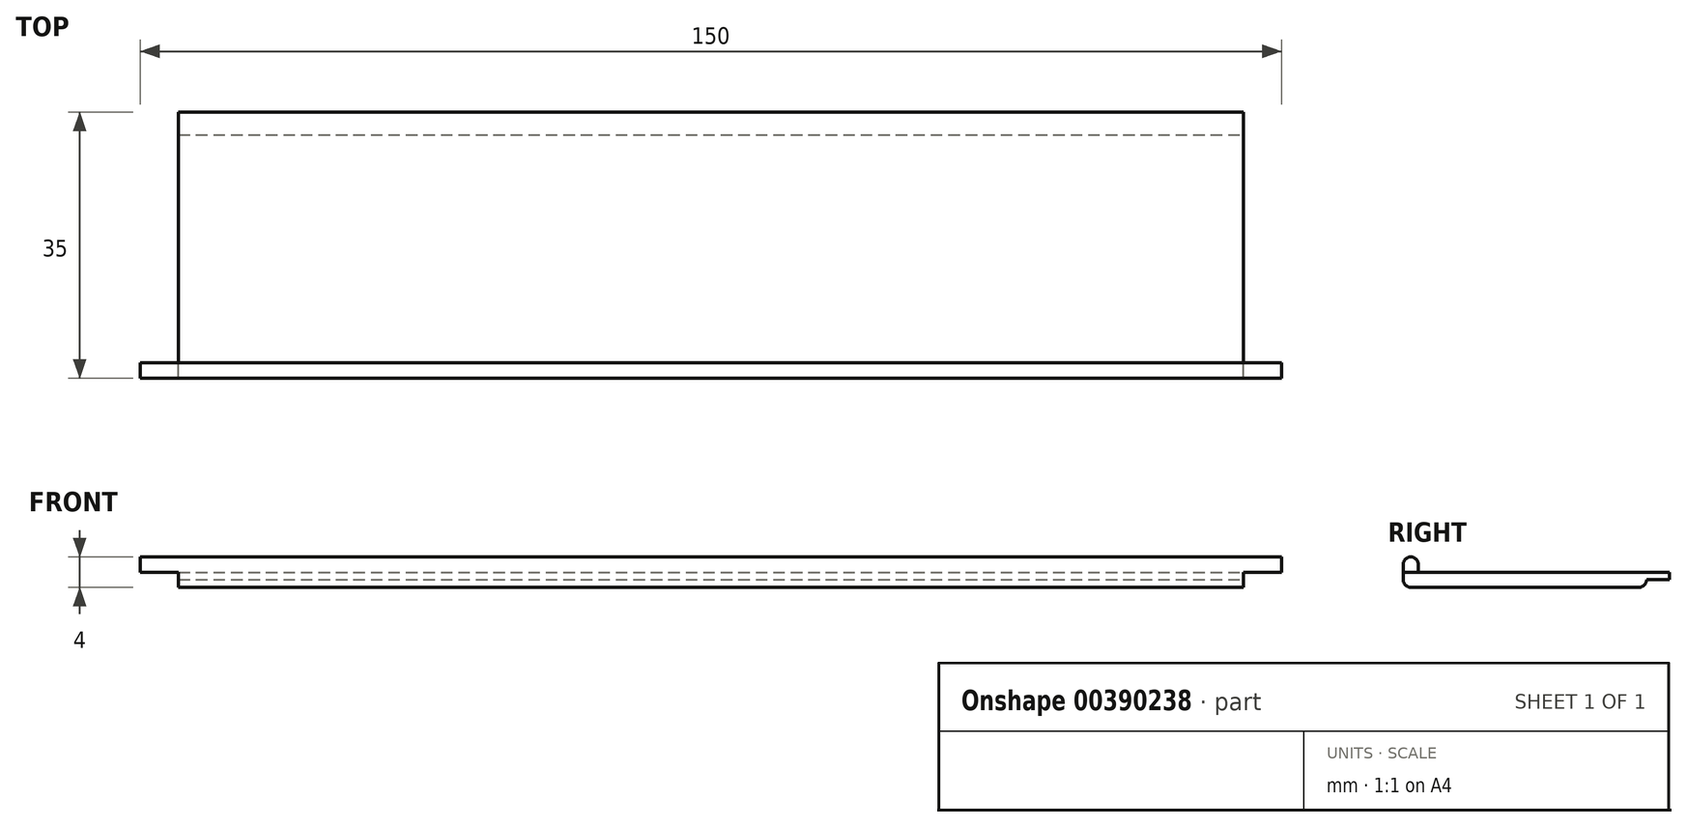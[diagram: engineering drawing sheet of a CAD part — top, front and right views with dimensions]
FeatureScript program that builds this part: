
annotation { "Feature Type Name" : "Feature", "Feature Type Description" : "" }
export const myFeature = defineFeature(function(context is Context, id is Id, definition is map)
    precondition{}
    {
        {
            var Q0;
            Q0=qCreatedBy(makeId("Right.planeOp"),FACE);
            var sketch = newSketch(context, id + "F0", { "sketchPlane" : qUnion([Q0])});
            skLineSegment(sketch, "E0.bottom", {"start": v(1, 0) * mm, "end": v(31, 0) * mm});
            skLineSegment(sketch, "E0.left", {"start": v(0, 1) * mm, "end": v(0, 1) * mm});
            skLineSegment(sketch, "E0.right", {"start": v(32, 1) * mm, "end": v(32, 1) * mm});
            skLineSegment(sketch, "E1.bottom", {"start": v(32, 1) * mm, "end": v(35, 1) * mm});
            skLineSegment(sketch, "E1.top", {"start": v(0, 2) * mm, "end": v(35, 2) * mm});
            skLineSegment(sketch, "E1.left", {"start": v(0, 1) * mm, "end": v(0, 2) * mm});
            skLineSegment(sketch, "E1.right", {"start": v(35, 1) * mm, "end": v(35, 2) * mm});
            skPoint(sketch, "E2.visualSharp", {"position": v(0, 0) * mm});
            skArc(sketch, "E2.filletArc", {"start": v(0, 1) * mm, "mid": v(0.3, 0.3) * mm, "end": v(1, 0) * mm});
            skPoint(sketch, "E3.visualSharp", {"position": v(32, 0) * mm});
            skArc(sketch, "E3.filletArc", {"start": v(31, 0) * mm, "mid": v(31.7, 0.3) * mm, "end": v(32, 1) * mm});
            skSolve(sketch);
        }
        {
            var Q0;
            Q0=qCreatedBy(makeId("Right.planeOp"),FACE);
            var sketch = newSketch(context, id + "F1", { "sketchPlane" : qUnion([Q0])});
            skLineSegment(sketch, "E4.bottom", {"start": v(0, 2) * mm, "end": v(2, 2) * mm});
            skLineSegment(sketch, "E4.top", {"start": v(1, 4) * mm, "end": v(1, 4) * mm});
            skLineSegment(sketch, "E4.left", {"start": v(0, 2) * mm, "end": v(0, 3) * mm});
            skLineSegment(sketch, "E4.right", {"start": v(2, 2) * mm, "end": v(2, 3) * mm});
            skPoint(sketch, "E5.visualSharp", {"position": v(0, 4) * mm});
            skArc(sketch, "E5.filletArc", {"start": v(1, 4) * mm, "mid": v(0.3, 3.7) * mm, "end": v(0, 3) * mm});
            skPoint(sketch, "E6.visualSharp", {"position": v(2, 4) * mm});
            skArc(sketch, "E6.filletArc", {"start": v(2, 3) * mm, "mid": v(1.7, 3.7) * mm, "end": v(1, 4) * mm});
            skSolve(sketch);
        }
        {
            var Q0;
            Q0=makeQuery(id+"F0.imprint","IMPRINT",FACE,{"disambiguationData":[TD([[makeQuery(id+"F0.imprint","IMPRINT",EDGE,{"derivedFrom":sQuery(id+"F0.wireOp",EDGE,"E0.bottom")}),1.0]])]});
            extrude(context, id + "F2", {"entities" : qUnion([Q0]), "depth" : -140 * mm});
        }
        {
            var Q0;
            Q0=makeQuery(id+"F1.imprint","IMPRINT",FACE,{"disambiguationData":[TD([[makeQuery(id+"F1.imprint","IMPRINT",EDGE,{"derivedFrom":sQuery(id+"F1.wireOp",EDGE,"E4.bottom")}),1.0]])]});
            extrude(context, id + "F3", {"entities" : qUnion([Q0]), "operationType" : NewBodyOperationType.ADD, "depth" : -145 * mm});
        }
        {
            var Q0;
            Q0 = qSketchRegion(id + "F1", true);
            extrude(context, id + "F4", {"entities" : qUnion([Q0]), "operationType" : NewBodyOperationType.ADD, "depth" : 5 * mm});
        }
    });
